# Revit family: Access_Door-Best-Access-Doors-BA-TLDF
name_source: partatom
category: Specialty Equipment
revit_build: Autodesk Revit 2017 (Build: 20160225_1515(x64)
units: mm (PartAtom-declared; Revit-internal decimal feet)

## family parameters
Cut with Voids When Loaded = No
Host = Face
OmniClass Number = 23.30.10.27.17
Part Type = Normal
Room Calculation Point = No
Round Connector Dimension = Use Diameter
Shared = No

## types (1)
- Not a Type - Load Type Catalog
    Assembly Code = C1020700
    Construction Material = Metal - Best Access Doors - Aluminum
    Default Elevation = 0"
    Description = Flush Access Door with Concealed Push-Latch and Drywall Flange
    Finish = Metal - Best Access Doors - Powder Coated White
    Frame Depth = 1 5/8"
    Height = 24"
    Height Actual = 26 1/4"
    Height C = 24"
    Manufacturer = Best Access Doors
    Material main = Powder coated steel
    Model = BA-TLDF
    Product data url = https://bimobject.com
    Type Comments = Please Load Accompanying .txt File
    URL = http://www.bestaccessdoors.com
    Version = 2015 – v1.0m
    Width = 24"
    Width Actual = 26 1/4"
    Width C = 24"

## geometry (parser evidence)
native form markers: Blend x4, Sweep x23
no freeform markers — native parametric forms only
